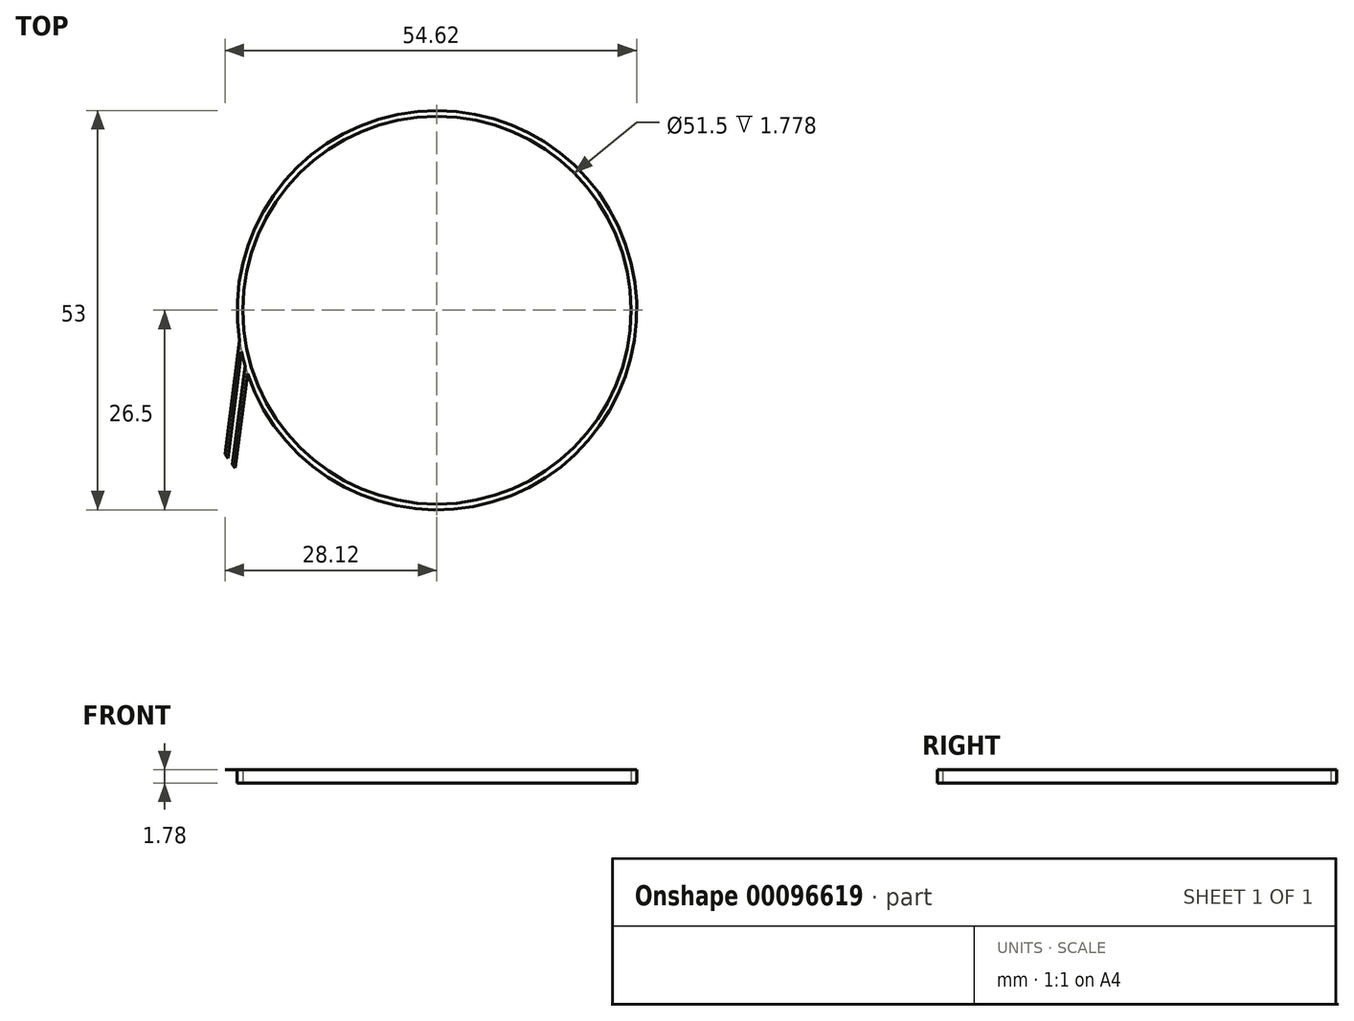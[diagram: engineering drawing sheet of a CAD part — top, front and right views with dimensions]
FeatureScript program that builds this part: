
annotation { "Feature Type Name" : "Feature", "Feature Type Description" : "" }
export const myFeature = defineFeature(function(context is Context, id is Id, definition is map)
    precondition{}
    {
        {
            var Q0;
            Q0=qCreatedBy(makeId("Top.planeOp"),FACE);
            var sketch = newSketch(context, id + "F0", { "sketchPlane" : qUnion([Q0])});
            skCircle(sketch, "E0", {"center": v(0, 0) * mm, "radius": 25.75 * mm});
            skCircle(sketch, "E1", {"center": v(0, 0) * mm, "radius": 26.5 * mm});
            skSolve(sketch);
        }
        {
            var Q0;
            Q0=makeQuery(id+"F0.imprint","IMPRINT",FACE,{"disambiguationData":[TD([[makeQuery(id+"F0.imprint","IMPRINT",EDGE,{"derivedFrom":sQuery(id+"F0.wireOp",EDGE,"E0")}),-1.0]])]});
            extrude(context, id + "F1", {"entities" : qUnion([Q0]), "depth" : 1.78 * mm});
        }
        {
            var Q0;
            Q0=makeQuery(id+"F1.opExtrude","CAP_FACE",FACE,{"disambiguationData":[OSD([sQuery(id+"F0.wireOp",EDGE,"E0"),sQuery(id+"F0.wireOp",EDGE,"E1")])],"isStart":false});
            var sketch = newSketch(context, id + "F2", { "sketchPlane" : qUnion([Q0])});
            skCircle(sketch, "E2", {"center": v(0, 0) * mm, "radius": 34 * mm});
            skLineSegment(sketch, "E3", {"start": v(-26.19, -4.04) * mm, "end": v(-28.12, -19.12) * mm});
            skLineSegment(sketch, "E4", {"start": v(-25.59, -2.9) * mm, "end": v(-27.73, -19.68) * mm});
            skLineSegment(sketch, "E5", {"start": v(-25.45, -7.38) * mm, "end": v(-27.13, -20.5) * mm});
            skLineSegment(sketch, "E6", {"start": v(-24.88, -6.63) * mm, "end": v(-26.8, -20.93) * mm});
            skLineSegment(sketch, "E7", {"start": v(-26.19, -4.04) * mm, "end": v(-25.59, -2.9) * mm});
            skLineSegment(sketch, "E8", {"start": v(-25.45, -7.38) * mm, "end": v(-24.88, -6.63) * mm});
            skLineSegment(sketch, "E9", {"start": v(-26.8, -20.93) * mm, "end": v(-27.13, -20.5) * mm});
            skLineSegment(sketch, "E10", {"start": v(-27.73, -19.68) * mm, "end": v(-28.12, -19.12) * mm});
            skSolve(sketch);
        }
        {
            var Q0;
            {var subQ0=sQuery(id+"F2.wireOp",EDGE,"E3");Q0=makeQuery(id+"F2.imprint","IMPRINT",FACE,{"disambiguationData":[TD([[makeQuery(id+"F2.imprint","IMPRINT",EDGE,{"derivedFrom":subQ0}),1.0]])]});}
            var Q1;
            {var subQ0=sQuery(id+"F2.wireOp",EDGE,"E5");Q1=makeQuery(id+"F2.imprint","IMPRINT",FACE,{"disambiguationData":[TD([[makeQuery(id+"F2.imprint","IMPRINT",EDGE,{"derivedFrom":subQ0}),1.0]])]});}
            extrude(context, id + "F3", {"entities" : qUnion([Q0, Q1]), "operationType" : NewBodyOperationType.ADD, "oppositeDirection" : true, "depth" : 0.03 * mm});
        }
    });
